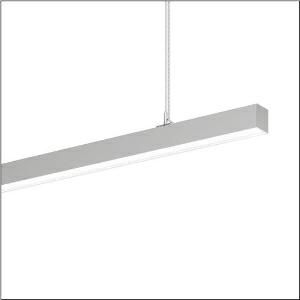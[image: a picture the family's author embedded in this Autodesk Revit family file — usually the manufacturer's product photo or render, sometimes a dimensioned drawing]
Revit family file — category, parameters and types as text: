
# Revit family: silica_r__21_51mx33tbt9s_9dae
name_source: partatom
category: Lighting Fixtures
units: mm (PartAtom-declared; Revit-internal decimal feet)

## family parameters
Cut with Voids When Loaded = No
Host = Face
Light Source = No
Part Type = Normal
Room Calculation Point = No
Round Connector Dimension = Use Diameter
Shared = No

## types (1)
- --- (1 x LED, 7170 lm, 67.4 W, 6500K)
    Apparent Load = 67 VA
    CIE Flux Codes = 78 96 99 56 100
    Color Rendering = 80
    Color Temperature = 6500K
    Default Elevation = 1800 mm
    Description = Silica® 21, office luminaire, primary optical cover: prismatic diffuser, of PMMA, CAT 2 (L<= 3000cd/m²), light emission: direct/indirect distribution, primary light characteristic: symmetric, installation type: suspended mounting, LED, rated luminous flux: 7.170lm, luminous efficacy: 101lm/W, light colour: 8tw, colour temperature: 2700..6500K, control gear: ECG DALI, with terminal, 3+2-pole, max. 2.5mm², mains connection: 220..240V, AC, 50/60Hz, rated input power: 70.8W, luminaire housing, of aluminium, metallic grey (RAL 9006), length: 1.504mm, width: 53mm, height: 53mm, protection rating (complete): IP20, insulation class (complete): insulation class I (protective earthing), certification: CE, permissible operating ambient temperature: 0..+35°C, standard: EN 50419, packaging unit: 1 piece
    Height = 53 mm
    Lamp = 1 x LED
    Lamp Light Flux = 7170 lm
    Lamp Power = 67.4 W
    Lamp count = 1
    Length = 1504 mm
    Luminous efficacy = 106 lm/W
    Manufacturer = Siteco
    ModVariant = No
    Model = 51MX33TBT9S
    Mounting Place = Ceiling
    Mounting Type = Pendant
    Number of Poles = 1
    OnlyDefault = Yes
    Power Factor = 1
    Product Name = Silica® 21
    Product group = office luminaire | ceiling pendant
    ProductGroupID = 902
    Protection Class = Protection class I
    Protection Degree = IP 20
    RLX_Detail_Level = 1
    RLX_Emergency_Light_Flux = 0 lm
    RLX_Emergency_Type = 0
    RLX_Emergency_Type_DB = No
    RlxData = <blob elided: 20213 chars, md5=e9e5391b>
    Socket = socket
    Standby Power = 0 W
    System Light Flux = 7170 lm
    System Power = 67 W
    Type Comments = individual setting
    Type Image = l_1297747.jpg
    URL = http://relux.com
    VarID = @adj_071065
    Voltage = 0 V
    Weight = 0.00 kg
    Width = 53 mm

## geometry (parser evidence)
native form markers: Blend x4, Sweep x13
no freeform markers — native parametric forms only
